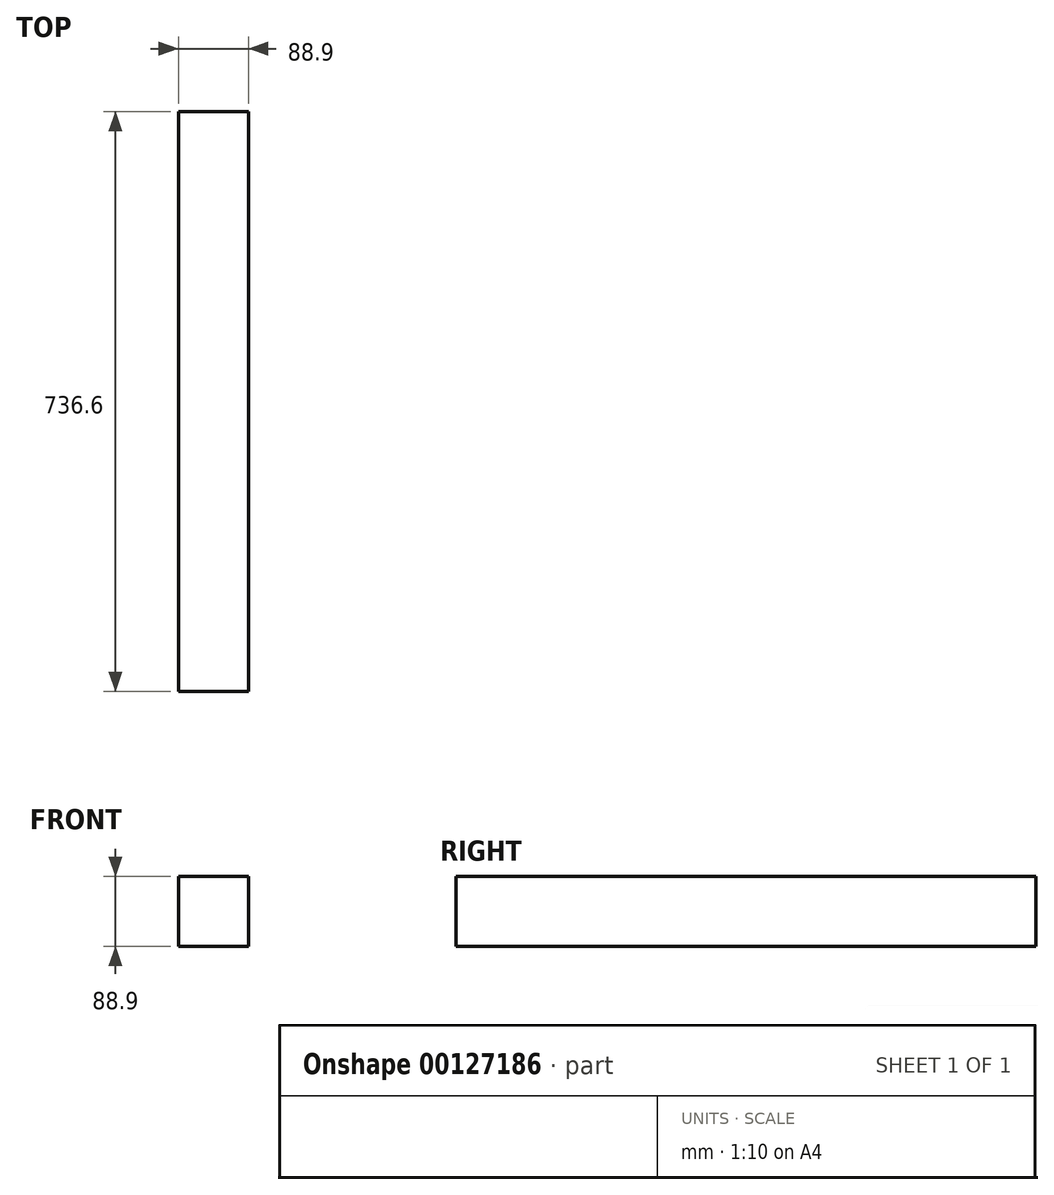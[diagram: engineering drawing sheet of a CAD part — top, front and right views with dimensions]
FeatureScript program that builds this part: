
annotation { "Feature Type Name" : "Feature", "Feature Type Description" : "" }
export const myFeature = defineFeature(function(context is Context, id is Id, definition is map)
    precondition{}
    {
        {
            var Q0;
            Q0=qCreatedBy(makeId("Front.planeOp"),FACE);
            var sketch = newSketch(context, id + "F0", { "sketchPlane" : qUnion([Q0])});
            skLineSegment(sketch, "E0.bottom", {"start": v(44.45, -44.45) * mm, "end": v(-44.45, -44.45) * mm});
            skLineSegment(sketch, "E0.top", {"start": v(44.45, 44.45) * mm, "end": v(-44.45, 44.45) * mm});
            skLineSegment(sketch, "E0.left", {"start": v(44.45, -44.45) * mm, "end": v(44.45, 44.45) * mm});
            skLineSegment(sketch, "E0.right", {"start": v(-44.45, -44.45) * mm, "end": v(-44.45, 44.45) * mm});
            skPoint(sketch, "E0.middle", {"position": v(0, 0) * mm});
            skSolve(sketch);
        }
        {
            var Q0;
            Q0=qSketchRegion(id+"F0",true);
            extrude(context, id + "F1", {"entities" : qUnion([Q0]), "depth" : 736.6 * mm});
        }
    });
